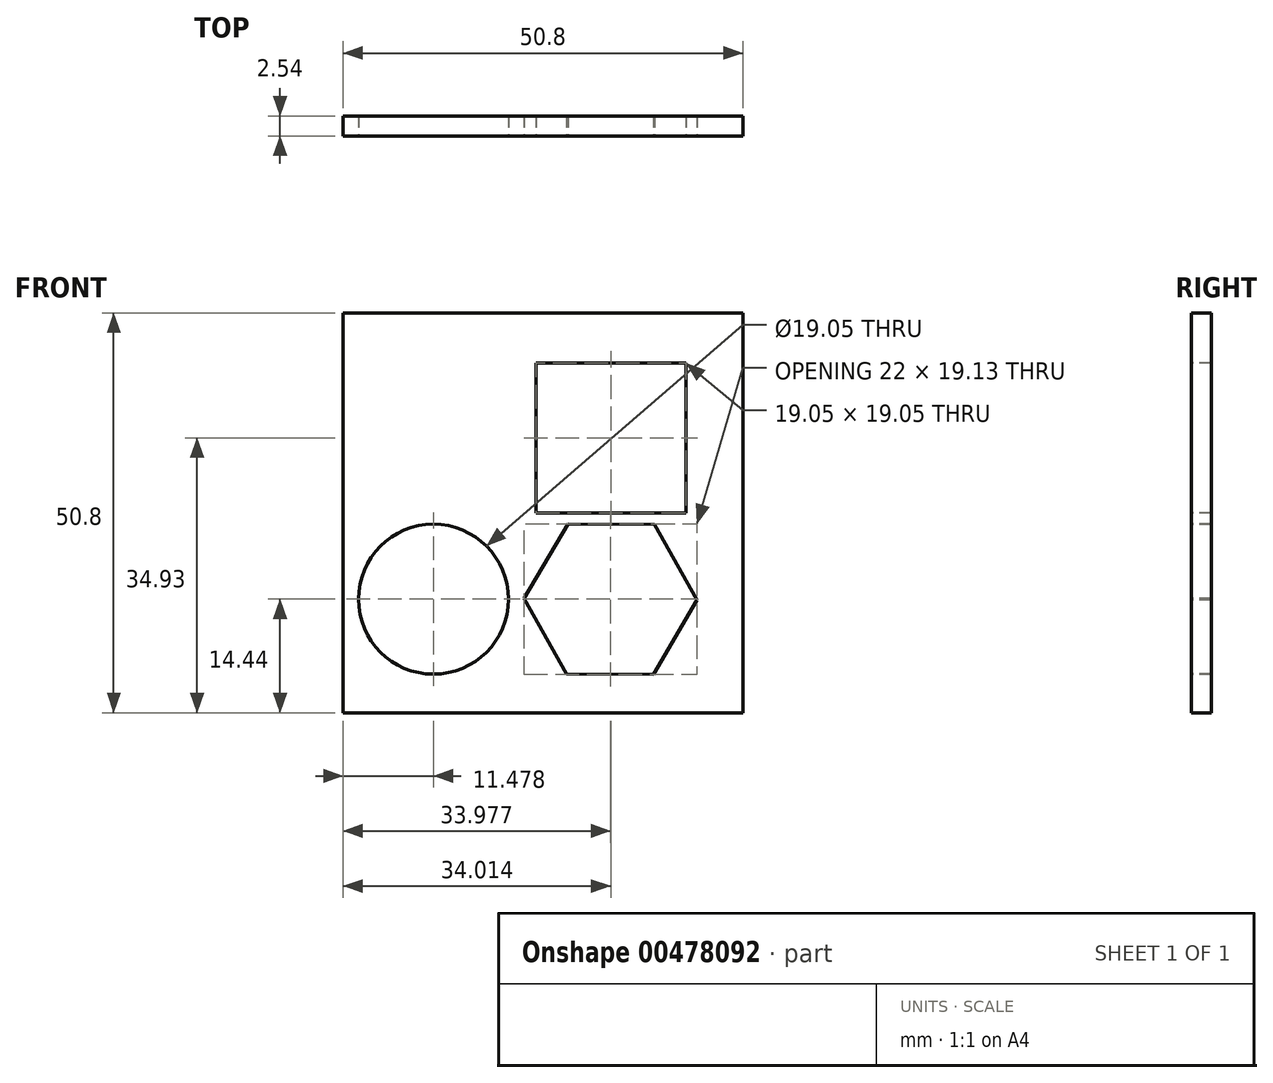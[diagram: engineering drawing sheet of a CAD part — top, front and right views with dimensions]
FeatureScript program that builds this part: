
annotation { "Feature Type Name" : "Feature", "Feature Type Description" : "" }
export const myFeature = defineFeature(function(context is Context, id is Id, definition is map)
    precondition{}
    {
        {
            var Q0;
            Q0=qCreatedBy(makeId("Front.planeOp"),FACE);
            var sketch = newSketch(context, id + "F0", { "sketchPlane" : qUnion([Q0])});
            skLineSegment(sketch, "E0.bottom", {"start": v(-59.85, 36.36) * mm, "end": v(-9.05, 36.36) * mm});
            skLineSegment(sketch, "E0.top", {"start": v(-59.85, -14.44) * mm, "end": v(-9.05, -14.44) * mm});
            skLineSegment(sketch, "E0.left", {"start": v(-59.85, 36.36) * mm, "end": v(-59.85, -14.44) * mm});
            skLineSegment(sketch, "E0.right", {"start": v(-9.05, 36.36) * mm, "end": v(-9.05, -14.44) * mm});
            skSolve(sketch);
        }
        {
            var Q0;
            Q0 = qSketchRegion(id + "F0", true);
            extrude(context, id + "F1", {"entities" : qUnion([Q0]), "depth" : 2.54 * mm});
        }
        {
            var Q0;
            Q0=makeQuery(id+"F1.opExtrude","CAP_FACE",FACE,{"disambiguationData":[OSD([sQuery(id+"F0.wireOp",EDGE,"E0.bottom"),sQuery(id+"F0.wireOp",EDGE,"E0.top"),sQuery(id+"F0.wireOp",EDGE,"E0.left"),sQuery(id+"F0.wireOp",EDGE,"E0.right")])],"isStart":false});
            var sketch = newSketch(context, id + "F2", { "sketchPlane" : qUnion([Q0])});
            skLineSegment(sketch, "E1.bottom", {"start": v(-35.36, 30.01) * mm, "end": v(-16.31, 30.01) * mm});
            skLineSegment(sketch, "E1.top", {"start": v(-35.36, 10.96) * mm, "end": v(-16.31, 10.96) * mm});
            skLineSegment(sketch, "E1.left", {"start": v(-35.36, 30.01) * mm, "end": v(-35.36, 10.96) * mm});
            skLineSegment(sketch, "E1.right", {"start": v(-16.31, 30.01) * mm, "end": v(-16.31, 10.96) * mm});
            skCircle(sketch, "E2", {"center": v(-48.37, 0) * mm, "radius": 9.53 * mm});
            skCircle(sketch, "E3.cCircle", {"center": v(-25.87, 0) * mm, "radius": 9.53 * mm, "construction": true});
            skLineSegment(sketch, "E3.0", {"start": v(-20.3, 9.49) * mm, "end": v(-14.87, -0.08) * mm});
            skLineSegment(sketch, "E3.1", {"start": v(-14.87, -0.08) * mm, "end": v(-20.44, -9.56) * mm});
            skLineSegment(sketch, "E3.2", {"start": v(-20.44, -9.56) * mm, "end": v(-31.44, -9.49) * mm});
            skLineSegment(sketch, "E3.3", {"start": v(-31.44, -9.49) * mm, "end": v(-36.87, 0.08) * mm});
            skLineSegment(sketch, "E3.4", {"start": v(-36.87, 0.08) * mm, "end": v(-31.3, 9.56) * mm});
            skLineSegment(sketch, "E3.5", {"start": v(-31.3, 9.56) * mm, "end": v(-20.3, 9.49) * mm});
            skPoint(sketch, "E3.0.midPoint", {"position": v(-17.6, 4.7) * mm});
            skSolve(sketch);
        }
        {
            var Q0;
            Q0 = qSketchRegion(id + "F2", true);
            extrude(context, id + "F3", {"entities" : qUnion([Q0]), "operationType" : NewBodyOperationType.REMOVE, "oppositeDirection" : true, "depth" : 25.4 * mm});
        }
    });
